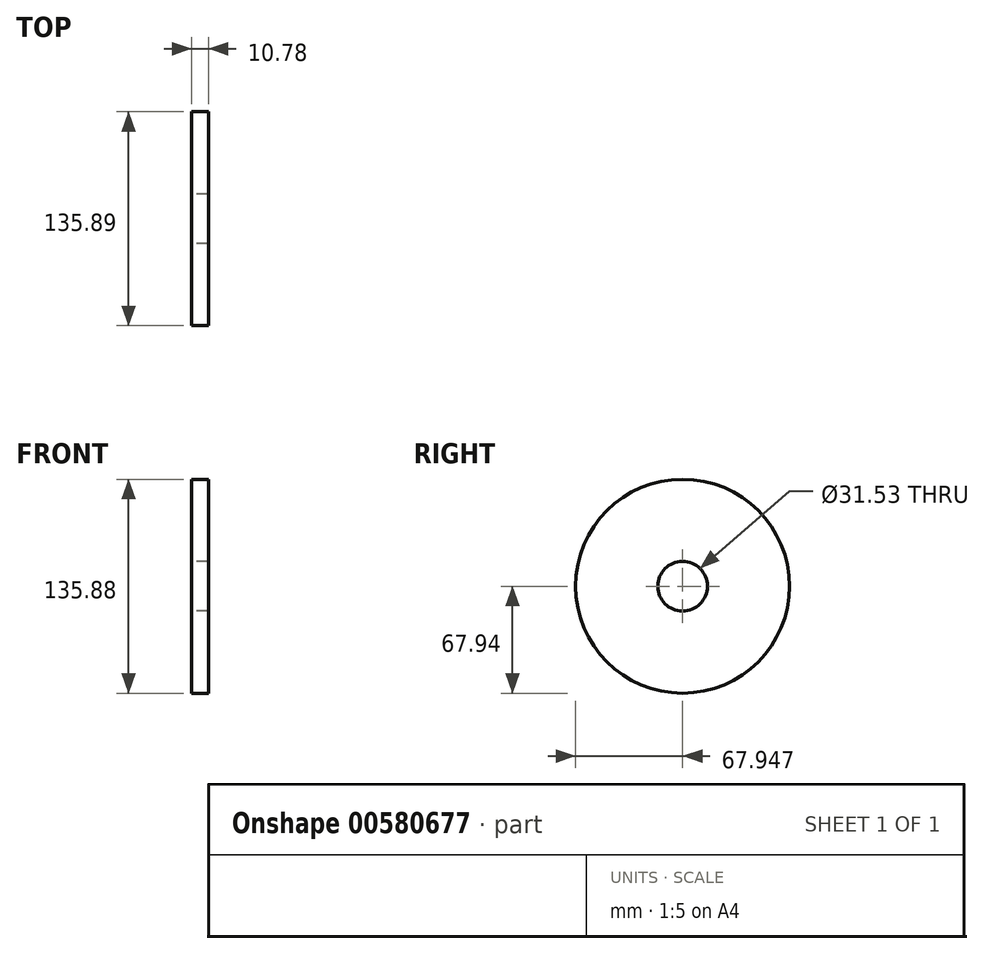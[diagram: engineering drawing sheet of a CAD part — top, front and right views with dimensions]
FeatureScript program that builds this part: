
annotation { "Feature Type Name" : "Feature", "Feature Type Description" : "" }
export const myFeature = defineFeature(function(context is Context, id is Id, definition is map)
    precondition{}
    {
        {
            var Q0;
            Q0=qCreatedBy(makeId("Top.planeOp"),FACE);
            var sketch = newSketch(context, id + "F0", { "sketchPlane" : qUnion([Q0])});
            skLineSegment(sketch, "E0", {"start": v(-62.42, 0) * mm, "end": v(69.72, 0) * mm});
            skLineSegment(sketch, "E1.bottom", {"start": v(-60.78, 0) * mm, "end": v(0, 0) * mm});
            skLineSegment(sketch, "E1.top", {"start": v(-60.78, 35.31) * mm, "end": v(0, 35.31) * mm});
            skLineSegment(sketch, "E1.left", {"start": v(-60.78, 0) * mm, "end": v(-60.78, 35.31) * mm});
            skLineSegment(sketch, "E1.right", {"start": v(0, 0) * mm, "end": v(0, 35.31) * mm});
            skLineSegment(sketch, "E2.bottom", {"start": v(-60.78, 0) * mm, "end": v(-71.56, 0) * mm});
            skLineSegment(sketch, "E2.top", {"start": v(-60.78, 52.18) * mm, "end": v(-71.56, 52.18) * mm});
            skLineSegment(sketch, "E2.left", {"start": v(-60.78, 0) * mm, "end": v(-60.78, 52.18) * mm});
            skLineSegment(sketch, "E2.right", {"start": v(-71.56, 0) * mm, "end": v(-71.56, 52.18) * mm});
            skLineSegment(sketch, "E3", {"start": v(-71.56, -15.76) * mm, "end": v(69.72, -15.76) * mm});
            skSolve(sketch);
        }
        {
            var Q0;
            {var subQ0=sQuery(id+"F0.wireOp",EDGE,"E1.bottom");Q0=makeQuery(id+"F0.imprint","IMPRINT",FACE,{"disambiguationData":[TD([[makeQuery(id+"F0.imprint","IMPRINT",EDGE,{"derivedFrom":subQ0}),1.0]])]});}
            var Q1;
            {var subQ2=sQuery(id+"F0.wireOp",EDGE,"E2.top");Q1=makeQuery(id+"F0.imprint","IMPRINT",FACE,{"disambiguationData":[TD([[makeQuery(id+"F0.imprint","IMPRINT",EDGE,{"derivedFrom":subQ2}),1.0]])]});}
            var Q2;
            Q2=sQuery(id+"F0.wireOp",EDGE,"E3");
            revolve(context, id + "F1", {"entities" : qUnion([Q0, Q1]), "axis" : qUnion([Q2]), "revolveType" : RevolveType.FULL});
        }
    });
